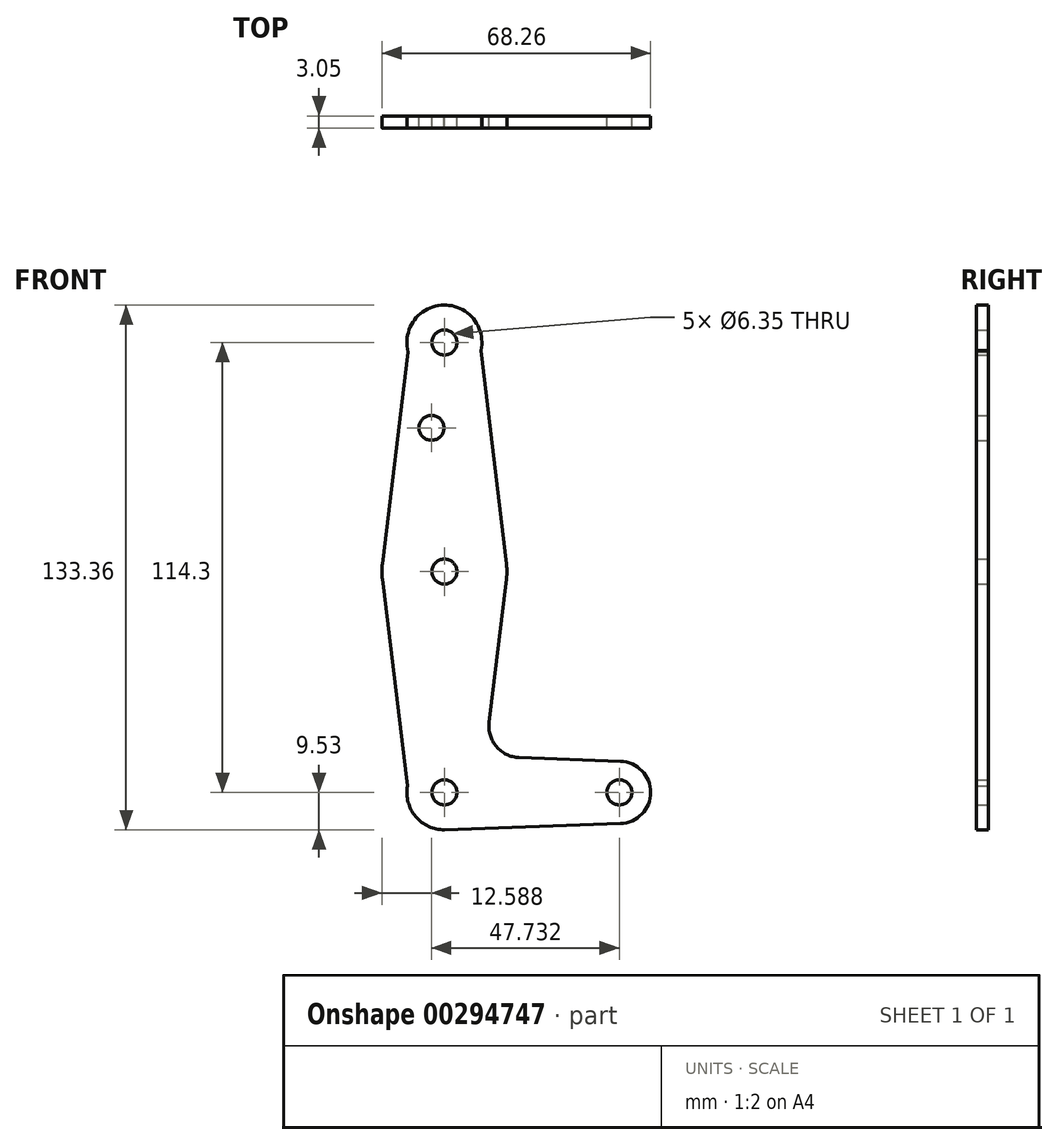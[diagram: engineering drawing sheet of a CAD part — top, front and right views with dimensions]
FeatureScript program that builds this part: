
annotation { "Feature Type Name" : "Feature", "Feature Type Description" : "" }
export const myFeature = defineFeature(function(context is Context, id is Id, definition is map)
    precondition{}
    {
        {
            var Q0;
            Q0=qCreatedBy(makeId("Front.planeOp"),FACE);
            var sketch = newSketch(context, id + "F0", { "sketchPlane" : qUnion([Q0])});
            skLineSegment(sketch, "E0", {"start": v(0, 0) * mm, "end": v(44.45, 0) * mm, "construction": true});
            skCircle(sketch, "E1", {"center": v(0, 114.3) * mm, "radius": 9.53 * mm});
            skCircle(sketch, "E2", {"center": v(0, 56.1) * mm, "radius": 15.88 * mm});
            skCircle(sketch, "E3", {"center": v(0, 0) * mm, "radius": 9.53 * mm});
            skCircle(sketch, "E4", {"center": v(44.45, 0) * mm, "radius": 7.94 * mm});
            skLineSegment(sketch, "E5", {"start": v(0, 114.3) * mm, "end": v(0, 0) * mm, "construction": true});
            skLineSegment(sketch, "E6", {"start": v(-9.23, 111.93) * mm, "end": v(-15.76, 58.01) * mm});
            skLineSegment(sketch, "E7", {"start": v(9.31, 112.3) * mm, "end": v(15.76, 57.97) * mm});
            skLineSegment(sketch, "E8", {"start": v(-15.76, 54.2) * mm, "end": v(-9.39, 1.6) * mm});
            skPoint(sketch, "E9.visualSharp", {"position": v(9.48, -0.91) * mm});
            skLineSegment(sketch, "E10", {"start": v(0, -9.53) * mm, "end": v(44.73, -7.93) * mm});
            skLineSegment(sketch, "E11", {"start": v(15.76, 54.23) * mm, "end": v(11.38, 17.74) * mm});
            skLineSegment(sketch, "E12", {"start": v(18.99, 8.85) * mm, "end": v(44.73, 7.93) * mm});
            skPoint(sketch, "E13.newPointB", {"position": v(0, 9.53) * mm});
            skArc(sketch, "E13.filletArc", {"start": v(11.38, 17.74) * mm, "mid": v(13.23, 11.63) * mm, "end": v(18.99, 8.85) * mm});
            skCircle(sketch, "E14", {"center": v(0, 114.3) * mm, "radius": 3.18 * mm});
            skCircle(sketch, "E15", {"center": v(0, 56.1) * mm, "radius": 3.18 * mm});
            skCircle(sketch, "E16", {"center": v(0, 0) * mm, "radius": 3.18 * mm});
            skCircle(sketch, "E17", {"center": v(44.45, 0) * mm, "radius": 3.18 * mm});
            skCircle(sketch, "E18", {"center": v(-3.28, 92.63) * mm, "radius": 3.18 * mm});
            skSolve(sketch);
        }
        {
            var Q0;
            Q0=makeQuery(id+"F0.imprint","IMPRINT",FACE,{"disambiguationData":[TD([[makeQuery(id+"F0.imprint","IMPRINT",EDGE,{"derivedFrom":sQuery(id+"F0.wireOp",EDGE,"E14")}),-1.0]])]});
            var Q1;
            {var subQ0=sQuery(id+"F0.wireOp",EDGE,"E6");Q1=makeQuery(id+"F0.imprint","IMPRINT",FACE,{"disambiguationData":[TD([[makeQuery(id+"F0.imprint","IMPRINT",EDGE,{"derivedFrom":subQ0}),1.0]])]});}
            var Q2;
            Q2=makeQuery(id+"F0.imprint","IMPRINT",FACE,{"disambiguationData":[TD([[makeQuery(id+"F0.imprint","IMPRINT",EDGE,{"derivedFrom":sQuery(id+"F0.wireOp",EDGE,"E15")}),-1.0]])]});
            var Q3;
            {var subQ0=sQuery(id+"F0.wireOp",EDGE,"E8");Q3=makeQuery(id+"F0.imprint","IMPRINT",FACE,{"disambiguationData":[TD([[makeQuery(id+"F0.imprint","IMPRINT",EDGE,{"derivedFrom":subQ0}),1.0]])]});}
            var Q4;
            Q4=makeQuery(id+"F0.imprint","IMPRINT",FACE,{"disambiguationData":[TD([[makeQuery(id+"F0.imprint","IMPRINT",EDGE,{"derivedFrom":sQuery(id+"F0.wireOp",EDGE,"E16")}),-1.0]])]});
            var Q5;
            Q5=makeQuery(id+"F0.imprint","IMPRINT",FACE,{"disambiguationData":[TD([[makeQuery(id+"F0.imprint","IMPRINT",EDGE,{"derivedFrom":sQuery(id+"F0.wireOp",EDGE,"E17")}),-1.0]])]});
            extrude(context, id + "F1", {"entities" : qUnion([Q0, Q1, Q2, Q3, Q4, Q5]), "depth" : 3.05 * mm});
        }
    });
